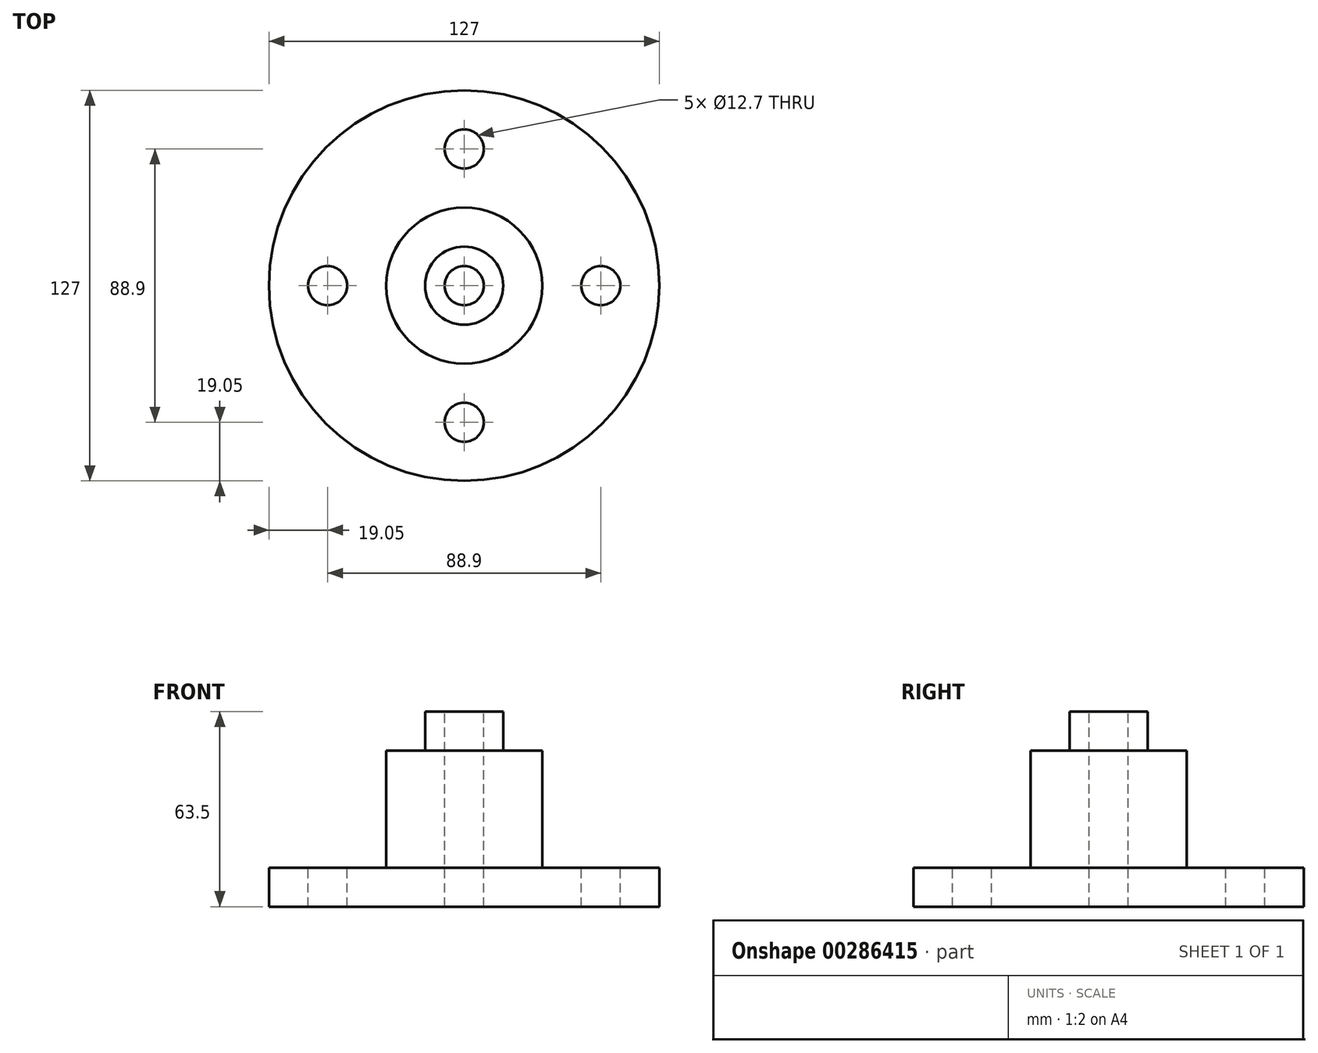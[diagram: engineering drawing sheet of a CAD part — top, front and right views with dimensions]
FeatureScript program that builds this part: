
annotation { "Feature Type Name" : "Feature", "Feature Type Description" : "" }
export const myFeature = defineFeature(function(context is Context, id is Id, definition is map)
    precondition{}
    {
        {
            var Q0;
            Q0=qCreatedBy(makeId("Top.planeOp"),FACE);
            var sketch = newSketch(context, id + "F0", { "sketchPlane" : qUnion([Q0])});
            skCircle(sketch, "E0", {"center": v(0, 0) * mm, "radius": 63.5 * mm});
            skSolve(sketch);
        }
        {
            var Q0;
            Q0=makeQuery(id+"F0.imprint","IMPRINT",FACE,{"disambiguationData":[TD([[makeQuery(id+"F0.imprint","IMPRINT",EDGE,{"derivedFrom":sQuery(id+"F0.wireOp",EDGE,"E0")}),1.0]])]});
            extrude(context, id + "F1", {"entities" : qUnion([Q0]), "depth" : 6.35 * mm});
        }
        {
            var Q0;
            Q0=makeQuery(id+"F1.opExtrude","CAP_FACE",FACE,{"disambiguationData":[OSD([sQuery(id+"F0.wireOp",EDGE,"E0")])],"isStart":true});
            extrude(context, id + "F2", {"entities" : qUnion([Q0]), "operationType" : NewBodyOperationType.ADD, "depth" : 6.35 * mm});
        }
        {
            var Q0;
            Q0=makeQuery(id+"F1.opExtrude","CAP_FACE",FACE,{"disambiguationData":[OSD([sQuery(id+"F0.wireOp",EDGE,"E0")])],"isStart":false});
            var sketch = newSketch(context, id + "F3", { "sketchPlane" : qUnion([Q0])});
            skCircle(sketch, "E1", {"center": v(0, 0) * mm, "radius": 25.4 * mm});
            skCircle(sketch, "E2", {"center": v(44.45, 0) * mm, "radius": 6.35 * mm});
            skCircle(sketch, "E3", {"center": v(0, 44.45) * mm, "radius": 6.35 * mm});
            skCircle(sketch, "E4", {"center": v(-44.45, 0) * mm, "radius": 6.35 * mm});
            skCircle(sketch, "E5", {"center": v(0, -44.45) * mm, "radius": 6.35 * mm});
            skSolve(sketch);
        }
        {
            var Q0;
            Q0=makeQuery(id+"F3.imprint","IMPRINT",FACE,{"disambiguationData":[TD([[makeQuery(id+"F3.imprint","IMPRINT",EDGE,{"derivedFrom":sQuery(id+"F3.wireOp",EDGE,"E4")}),1.0]])]});
            var Q1;
            Q1=makeQuery(id+"F3.imprint","IMPRINT",FACE,{"disambiguationData":[TD([[makeQuery(id+"F3.imprint","IMPRINT",EDGE,{"derivedFrom":sQuery(id+"F3.wireOp",EDGE,"E3")}),1.0]])]});
            var Q2;
            Q2=makeQuery(id+"F3.imprint","IMPRINT",FACE,{"disambiguationData":[TD([[makeQuery(id+"F3.imprint","IMPRINT",EDGE,{"derivedFrom":sQuery(id+"F3.wireOp",EDGE,"E2")}),1.0]])]});
            var Q3;
            Q3=makeQuery(id+"F3.imprint","IMPRINT",FACE,{"disambiguationData":[TD([[makeQuery(id+"F3.imprint","IMPRINT",EDGE,{"derivedFrom":sQuery(id+"F3.wireOp",EDGE,"E5")}),1.0]])]});
            extrude(context, id + "F4", {"entities" : qUnion([Q0, Q1, Q2, Q3]), "operationType" : NewBodyOperationType.REMOVE, "oppositeDirection" : true, "depth" : 12.7 * mm});
        }
        {
            var Q0;
            Q0=makeQuery(id+"F3.imprint","IMPRINT",FACE,{"disambiguationData":[TD([[makeQuery(id+"F3.imprint","IMPRINT",EDGE,{"derivedFrom":sQuery(id+"F3.wireOp",EDGE,"E1")}),1.0]])]});
            extrude(context, id + "F5", {"entities" : qUnion([Q0]), "operationType" : NewBodyOperationType.ADD, "depth" : 38.1 * mm});
        }
        {
            var Q0;
            Q0=makeQuery(id+"F5.opExtrude","CAP_FACE",FACE,{"disambiguationData":[OSD([sQuery(id+"F3.wireOp",EDGE,"E1")])],"isStart":false});
            var sketch = newSketch(context, id + "F6", { "sketchPlane" : qUnion([Q0])});
            skCircle(sketch, "E6", {"center": v(0, 0) * mm, "radius": 12.7 * mm});
            skSolve(sketch);
        }
        {
            var Q0;
            Q0=makeQuery(id+"F6.imprint","IMPRINT",FACE,{"disambiguationData":[TD([[makeQuery(id+"F6.imprint","IMPRINT",EDGE,{"derivedFrom":sQuery(id+"F6.wireOp",EDGE,"E6")}),1.0]])]});
            extrude(context, id + "F7", {"entities" : qUnion([Q0]), "operationType" : NewBodyOperationType.ADD, "depth" : 12.7 * mm});
        }
        {
            var Q0;
            Q0=makeQuery(id+"F7.opExtrude","CAP_FACE",FACE,{"disambiguationData":[OSD([sQuery(id+"F6.wireOp",EDGE,"E6")])],"isStart":false});
            var sketch = newSketch(context, id + "F8", { "sketchPlane" : qUnion([Q0])});
            skCircle(sketch, "E7", {"center": v(0, 0) * mm, "radius": 6.35 * mm});
            skSolve(sketch);
        }
        {
            var Q0;
            Q0=makeQuery(id+"F8.imprint","IMPRINT",FACE,{"disambiguationData":[TD([[makeQuery(id+"F8.imprint","IMPRINT",EDGE,{"derivedFrom":sQuery(id+"F8.wireOp",EDGE,"E7")}),1.0]])]});
            extrude(context, id + "F9", {"entities" : qUnion([Q0]), "operationType" : NewBodyOperationType.REMOVE, "oppositeDirection" : true, "depth" : 63.5 * mm});
        }
    });
